# Revit family: Qf_Summit_AFS49ML_Pharma_Lab_All_Freezer
name_source: partatom
category: Specialty Equipment
units: mm (PartAtom-declared; Revit-internal decimal feet)

## family parameters
Always vertical = Yes
Cut with Voids When Loaded = No
Part Type = Normal
Room Calculation Point = No
Round Connector Dimension = Use Diameter
Shared = Yes
Work Plane-Based = No

## types (1)
- Qf_Summit_AFS49ML_Pharma_Lab_All_Freezer
    Apparent Power = 1208 VA
    Conn Conduit = Yes
    Cycle = 60 Hz
    Default Elevation = 0"
    Depth = 31"
    Description = Pharma-Lab All-Freezer
    Elec Conn RI Height = 0"
    FL Amps = 11 A
    Height = 83 3/4"
    Length = 55 1/4"
    Manufacturer = Summit
    Max Overcurrent Protection = 0 A
    Min Ckt Ampacity = 0 A
    Model = AFS49ML
    Phase = 1
    Refrigerant Type = R290a
    URL = www.summitappliance.com
    URL Cutsheet = www.summitappliance.com
    URL Manufacturer = www.summitappliance.com
    Volts = 115 V
    Watts = 1208 W
    Weight in Pounds = 428

## geometry (parser evidence)
native form markers: Blend x12, Sweep x5
no freeform markers — native parametric forms only
